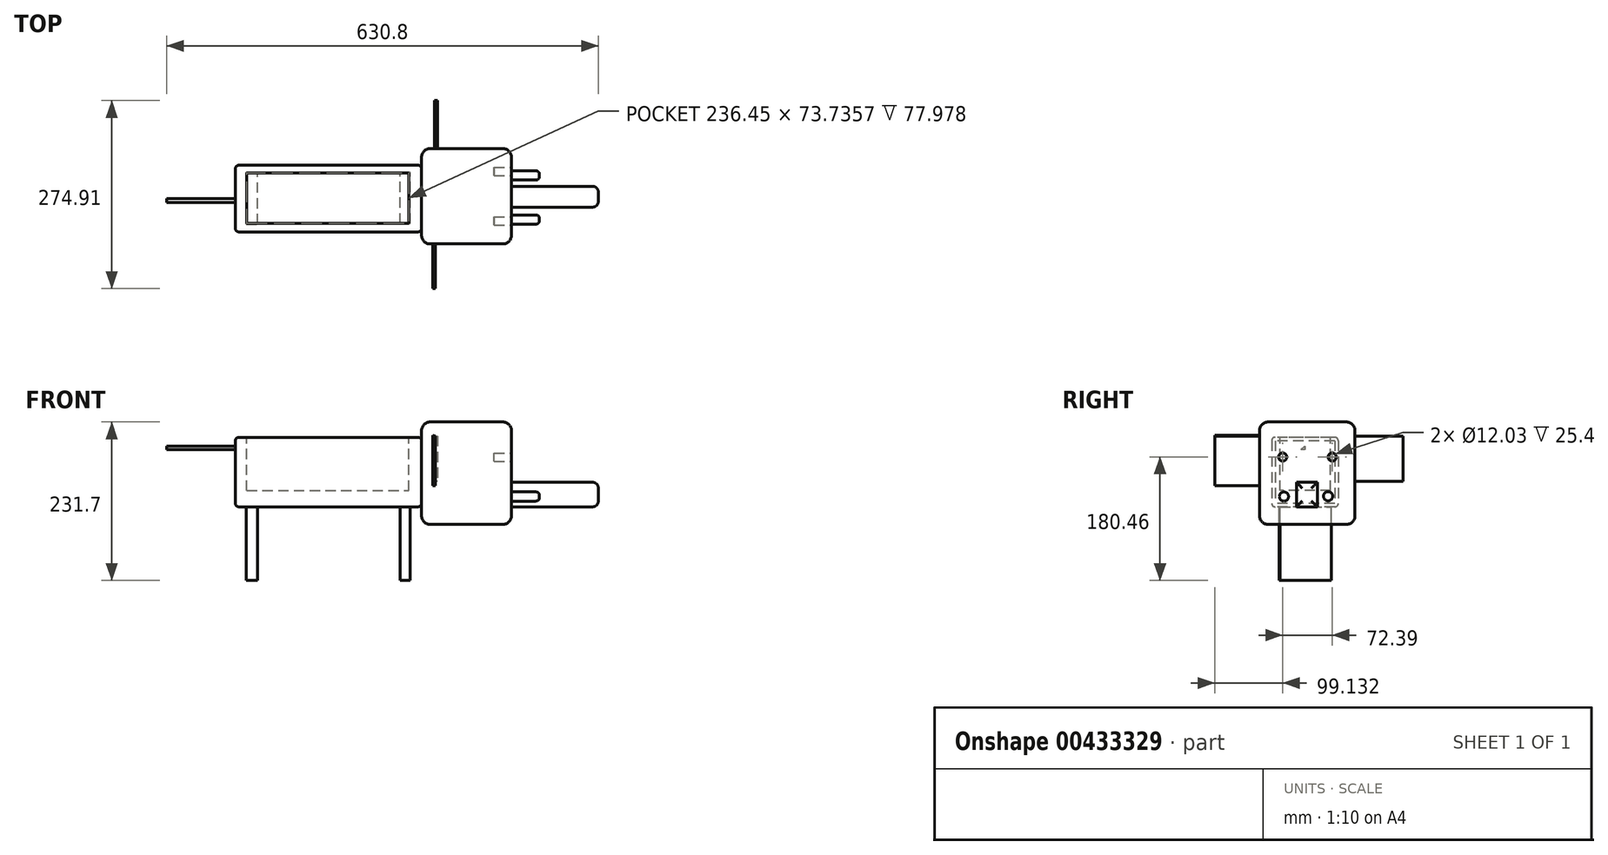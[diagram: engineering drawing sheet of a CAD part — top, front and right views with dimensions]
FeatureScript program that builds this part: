
annotation { "Feature Type Name" : "Feature", "Feature Type Description" : "" }
export const myFeature = defineFeature(function(context is Context, id is Id, definition is map)
    precondition{}
    {
        {
            var Q0;
            Q0=qCreatedBy(makeId("Top.planeOp"),FACE);
            var sketch = newSketch(context, id + "F0", { "sketchPlane" : qUnion([Q0])});
            skLineSegment(sketch, "E0.bottom", {"start": v(-125.37, 30.71) * mm, "end": v(146.52, 30.71) * mm});
            skLineSegment(sketch, "E0.top", {"start": v(-125.37, -66.73) * mm, "end": v(146.52, -66.73) * mm});
            skLineSegment(sketch, "E0.left", {"start": v(-125.37, 30.71) * mm, "end": v(-125.37, -66.73) * mm});
            skLineSegment(sketch, "E0.right", {"start": v(146.52, 30.71) * mm, "end": v(146.52, -66.73) * mm});
            skSolve(sketch);
        }
        {
            var Q0;
            Q0=makeQuery(id+"F0.imprint","IMPRINT",FACE,{"disambiguationData":[TD([[makeQuery(id+"F0.imprint","IMPRINT",EDGE,{"derivedFrom":sQuery(id+"F0.wireOp",EDGE,"E0.bottom")}),-1.0]])]});
            extrude(context, id + "F1", {"entities" : qUnion([Q0]), "depth" : 101.6 * mm});
        }
        {
            var Q0;
            Q0=makeQuery(id+"F1.opExtrude","CAP_FACE",FACE,{"disambiguationData":[OSD([sQuery(id+"F0.wireOp",EDGE,"E0.bottom"),sQuery(id+"F0.wireOp",EDGE,"E0.top"),sQuery(id+"F0.wireOp",EDGE,"E0.left"),sQuery(id+"F0.wireOp",EDGE,"E0.right")])],"isStart":false});
            var sketch = newSketch(context, id + "F2", { "sketchPlane" : qUnion([Q0])});
            skLineSegment(sketch, "E1.bottom", {"start": v(-108.8, 19.56) * mm, "end": v(127.65, 19.56) * mm});
            skLineSegment(sketch, "E1.top", {"start": v(-108.8, -54.18) * mm, "end": v(127.65, -54.18) * mm});
            skLineSegment(sketch, "E1.left", {"start": v(-108.8, 19.56) * mm, "end": v(-108.8, -54.18) * mm});
            skLineSegment(sketch, "E1.right", {"start": v(127.65, 19.56) * mm, "end": v(127.65, -54.18) * mm});
            skSolve(sketch);
        }
        {
            var Q0;
            Q0=makeQuery(id+"F1.opExtrude","SWEPT_FACE",FACE,{"disambiguationData":[OSD([sQuery(id+"F0.wireOp",EDGE,"E0.top")])]});
            var Q1;
            Q1=makeQuery(id+"F1.opExtrude","SWEPT_FACE",FACE,{"disambiguationData":[OSD([sQuery(id+"F0.wireOp",EDGE,"E0.right")])]});
            var Q2;
            Q2=makeQuery(id+"F1.opExtrude","SWEPT_FACE",FACE,{"disambiguationData":[OSD([sQuery(id+"F0.wireOp",EDGE,"E0.bottom")])]});
            var Q3;
            Q3=makeQuery(id+"F1.opExtrude","SWEPT_FACE",FACE,{"disambiguationData":[OSD([sQuery(id+"F0.wireOp",EDGE,"E0.left")])]});
            var Q4;
            Q4=makeQuery(id+"F95bG39HBBs5OQX_1.opShell","OFFSET_FACE",FACE,{"disambiguationData":[OSD([sQuery(id+"F0.wireOp",EDGE,"E0.top")])]});
            var Q5;
            Q5=makeQuery(id+"F95bG39HBBs5OQX_1.opShell","OFFSET_FACE",FACE,{"disambiguationData":[OSD([sQuery(id+"F0.wireOp",EDGE,"E0.left")])]});
            var Q6;
            Q6=makeQuery(id+"F95bG39HBBs5OQX_1.opShell","OFFSET_FACE",FACE,{"disambiguationData":[OSD([sQuery(id+"F0.wireOp",EDGE,"E0.bottom")])]});
            var Q7;
            Q7=makeQuery(id+"F95bG39HBBs5OQX_1.opShell","OFFSET_FACE",FACE,{"disambiguationData":[OSD([sQuery(id+"F0.wireOp",EDGE,"E0.bottom"),sQuery(id+"F0.wireOp",EDGE,"E0.top"),sQuery(id+"F0.wireOp",EDGE,"E0.left"),sQuery(id+"F0.wireOp",EDGE,"E0.right")])]});
            fillet(context, id + "F3", {"entities" : qUnion([Q0, Q1, Q2, Q3, Q4, Q5, Q6, Q7]), "radius" : 5.08 * mm, "tangentPropagation" : true, "allowEdgeOverflow" : false});
        }
        {
            var Q0;
            Q0=makeQuery(id+"F1.opExtrude","CAP_FACE",FACE,{"disambiguationData":[OSD([sQuery(id+"F0.wireOp",EDGE,"E0.bottom"),sQuery(id+"F0.wireOp",EDGE,"E0.top"),sQuery(id+"F0.wireOp",EDGE,"E0.left"),sQuery(id+"F0.wireOp",EDGE,"E0.right")])],"isStart":true});
            var sketch = newSketch(context, id + "F4", { "sketchPlane" : qUnion([Q0])});
            skLineSegment(sketch, "E2.bottom", {"start": v(-109.59, 55.4) * mm, "end": v(-92.98, 55.4) * mm});
            skLineSegment(sketch, "E2.top", {"start": v(-109.59, -20.61) * mm, "end": v(-92.98, -20.61) * mm});
            skLineSegment(sketch, "E2.left", {"start": v(-109.59, 55.4) * mm, "end": v(-109.59, -20.61) * mm});
            skLineSegment(sketch, "E2.right", {"start": v(-92.98, 55.4) * mm, "end": v(-92.98, -20.61) * mm});
            skSolve(sketch);
        }
        {
            var Q0;
            Q0 = qSketchRegion(id + "F4", true);
            extrude(context, id + "F5", {"entities" : qUnion([Q0]), "operationType" : NewBodyOperationType.ADD, "depth" : 107.7 * mm});
        }
        {
            var Q0;
            Q0=makeQuery(id+"F1.opExtrude","CAP_FACE",FACE,{"disambiguationData":[OSD([sQuery(id+"F0.wireOp",EDGE,"E0.bottom"),sQuery(id+"F0.wireOp",EDGE,"E0.top"),sQuery(id+"F0.wireOp",EDGE,"E0.left"),sQuery(id+"F0.wireOp",EDGE,"E0.right")])],"isStart":true});
            var sketch = newSketch(context, id + "F6", { "sketchPlane" : qUnion([Q0])});
            skLineSegment(sketch, "E3.bottom", {"start": v(115.1, 54.41) * mm, "end": v(130.15, 54.41) * mm});
            skLineSegment(sketch, "E3.top", {"start": v(115.1, -20.42) * mm, "end": v(130.15, -20.42) * mm});
            skLineSegment(sketch, "E3.left", {"start": v(115.1, 54.41) * mm, "end": v(115.1, -20.42) * mm});
            skLineSegment(sketch, "E3.right", {"start": v(130.15, 54.41) * mm, "end": v(130.15, -20.42) * mm});
            skSolve(sketch);
        }
        {
            var Q0;
            Q0 = qSketchRegion(id + "F6", true);
            extrude(context, id + "F7", {"entities" : qUnion([Q0]), "operationType" : NewBodyOperationType.ADD, "depth" : 107.7 * mm});
        }
        {
            var Q0;
            Q0 = qSketchRegion(id + "F2", true);
            extrude(context, id + "F8", {"entities" : qUnion([Q0]), "operationType" : NewBodyOperationType.REMOVE, "oppositeDirection" : true, "depth" : 77.98 * mm});
        }
        {
            var Q0;
            Q0=makeQuery(id+"F1.opExtrude","SWEPT_FACE",FACE,{"disambiguationData":[OSD([sQuery(id+"F0.wireOp",EDGE,"E0.right")])]});
            var sketch = newSketch(context, id + "F9", { "sketchPlane" : qUnion([Q0])});
            skLineSegment(sketch, "E4.bottom", {"start": v(-84.42, 124) * mm, "end": v(55.11, 124) * mm});
            skLineSegment(sketch, "E4.top", {"start": v(-84.42, -25.73) * mm, "end": v(55.11, -25.73) * mm});
            skLineSegment(sketch, "E4.left", {"start": v(-84.42, 124) * mm, "end": v(-84.42, -25.73) * mm});
            skLineSegment(sketch, "E4.right", {"start": v(55.11, 124) * mm, "end": v(55.11, -25.73) * mm});
            skSolve(sketch);
        }
        {
            var Q0;
            Q0 = qSketchRegion(id + "F9", true);
            extrude(context, id + "F10", {"entities" : qUnion([Q0]), "operationType" : NewBodyOperationType.ADD, "depth" : 131.32 * mm});
        }
        {
            var Q0;
            Q0=makeQuery(id+"F10.opExtrude","SWEPT_FACE",FACE,{"disambiguationData":[OSD([sQuery(id+"F9.wireOp",EDGE,"E4.bottom")])]});
            var Q1;
            Q1=makeQuery(id+"F10.opExtrude","SWEPT_FACE",FACE,{"disambiguationData":[OSD([sQuery(id+"F9.wireOp",EDGE,"E4.left")])]});
            var Q2;
            Q2=makeQuery(id+"F10.opExtrude","CAP_FACE",FACE,{"disambiguationData":[OSD([sQuery(id+"F9.wireOp",EDGE,"E4.bottom"),sQuery(id+"F9.wireOp",EDGE,"E4.top"),sQuery(id+"F9.wireOp",EDGE,"E4.left"),sQuery(id+"F9.wireOp",EDGE,"E4.right")])],"isStart":false});
            var Q3;
            Q3=makeQuery(id+"F10.opExtrude","SWEPT_FACE",FACE,{"disambiguationData":[OSD([sQuery(id+"F9.wireOp",EDGE,"E4.right")])]});
            var Q4;
            Q4=makeQuery(id+"F10.opExtrude","SWEPT_FACE",FACE,{"disambiguationData":[OSD([sQuery(id+"F9.wireOp",EDGE,"E4.top")])]});
            fillet(context, id + "F11", {"entities" : qUnion([Q0, Q1, Q2, Q3, Q4]), "radius" : 12.7 * mm, "tangentPropagation" : true, "allowEdgeOverflow" : false});
        }
        {
            var Q0;
            Q0=makeQuery(id+"F10.opExtrude","CAP_FACE",FACE,{"disambiguationData":[OSD([sQuery(id+"F9.wireOp",EDGE,"E4.bottom"),sQuery(id+"F9.wireOp",EDGE,"E4.top"),sQuery(id+"F9.wireOp",EDGE,"E4.left"),sQuery(id+"F9.wireOp",EDGE,"E4.right")])],"isStart":false});
            var sketch = newSketch(context, id + "F12", { "sketchPlane" : qUnion([Q0])});
            skLineSegment(sketch, "E5.bottom", {"start": v(-30.55, 35.93) * mm, "end": v(0, 35.93) * mm});
            skLineSegment(sketch, "E5.top", {"start": v(-30.55, 0) * mm, "end": v(0, 0) * mm});
            skLineSegment(sketch, "E5.left", {"start": v(-30.55, 35.93) * mm, "end": v(-30.55, 0) * mm});
            skLineSegment(sketch, "E5.right", {"start": v(0, 35.93) * mm, "end": v(0, 0) * mm});
            skSolve(sketch);
        }
        {
            var Q0;
            Q0 = qSketchRegion(id + "F12", true);
            extrude(context, id + "F13", {"entities" : qUnion([Q0]), "operationType" : NewBodyOperationType.ADD, "depth" : 127 * mm});
        }
        {
            var Q0;
            Q0=makeQuery(id+"F10.opExtrude","SWEPT_FACE",FACE,{"disambiguationData":[OSD([sQuery(id+"F9.wireOp",EDGE,"E4.left")])]});
            var sketch = newSketch(context, id + "F14", { "sketchPlane" : qUnion([Q0])});
            skLineSegment(sketch, "E6", {"start": v(163.04, 104.45) * mm, "end": v(163.04, 30.65) * mm});
            skLineSegment(sketch, "E7", {"start": v(163.04, 30.65) * mm, "end": v(166.6, 30.65) * mm});
            skLineSegment(sketch, "E8", {"start": v(166.6, 30.65) * mm, "end": v(166.6, 103.47) * mm});
            skLineSegment(sketch, "E9", {"start": v(166.6, 103.47) * mm, "end": v(163.04, 104.45) * mm});
            skSolve(sketch);
        }
        {
            var Q0;
            Q0=makeQuery(id+"F14.imprint","IMPRINT",FACE,{"disambiguationData":[TD([[makeQuery(id+"F14.imprint","IMPRINT",EDGE,{"derivedFrom":sQuery(id+"F14.wireOp",EDGE,"E6")}),1.0]])]});
            extrude(context, id + "F15", {"entities" : qUnion([Q0]), "operationType" : NewBodyOperationType.ADD, "depth" : 65.28 * mm});
        }
        {
            var Q0;
            Q0=makeQuery(id+"F10.opExtrude","SWEPT_FACE",FACE,{"disambiguationData":[OSD([sQuery(id+"F9.wireOp",EDGE,"E4.right")])]});
            var sketch = newSketch(context, id + "F16", { "sketchPlane" : qUnion([Q0])});
            skLineSegment(sketch, "E10", {"start": v(-165.3, 103.36) * mm, "end": v(-170, 103.36) * mm});
            skLineSegment(sketch, "E11", {"start": v(-170, 103.36) * mm, "end": v(-170, 36.95) * mm});
            skLineSegment(sketch, "E12", {"start": v(-170, 36.95) * mm, "end": v(-165.8, 36.95) * mm});
            skLineSegment(sketch, "E13", {"start": v(-165.8, 36.95) * mm, "end": v(-165.3, 103.36) * mm});
            skSolve(sketch);
        }
        {
            var Q0;
            Q0 = qSketchRegion(id + "F16", true);
            extrude(context, id + "F17", {"entities" : qUnion([Q0]), "operationType" : NewBodyOperationType.ADD, "depth" : 70.1 * mm});
        }
        {
            var Q0;
            Q0=makeQuery(id+"F10.opExtrude","CAP_FACE",FACE,{"disambiguationData":[OSD([sQuery(id+"F9.wireOp",EDGE,"E4.bottom"),sQuery(id+"F9.wireOp",EDGE,"E4.top"),sQuery(id+"F9.wireOp",EDGE,"E4.left"),sQuery(id+"F9.wireOp",EDGE,"E4.right")])],"isStart":false});
            var sketch = newSketch(context, id + "F18", { "sketchPlane" : qUnion([Q0])});
            skCircle(sketch, "E14", {"center": v(-48.64, 15.07) * mm, "radius": 6.72 * mm});
            skCircle(sketch, "E15.1.0.0", {"center": v(15.75, 15.5) * mm, "radius": 6.72 * mm});
            skLineSegment(sketch, "E15.direction1", {"start": v(-48.64, 15.07) * mm, "end": v(15.75, 15.5) * mm, "construction": true});
            skSolve(sketch);
        }
        {
            var Q0;
            Q0 = qSketchRegion(id + "F18", true);
            extrude(context, id + "F19", {"entities" : qUnion([Q0]), "operationType" : NewBodyOperationType.ADD, "depth" : 40.9 * mm});
        }
        {
            var Q0;
            Q0=makeQuery(id+"F1.opExtrude","SWEPT_FACE",FACE,{"disambiguationData":[OSD([sQuery(id+"F0.wireOp",EDGE,"E0.left")])]});
            var sketch = newSketch(context, id + "F20", { "sketchPlane" : qUnion([Q0])});
            skLineSegment(sketch, "E16", {"start": v(17.9, 88.55) * mm, "end": v(17.9, 83.87) * mm});
            skLineSegment(sketch, "E17", {"start": v(17.9, 83.87) * mm, "end": v(23.7, 83.87) * mm});
            skLineSegment(sketch, "E18", {"start": v(23.7, 83.87) * mm, "end": v(17.9, 88.55) * mm});
            skSolve(sketch);
        }
        {
            var Q0;
            Q0 = qSketchRegion(id + "F20", true);
            extrude(context, id + "F21", {"entities" : qUnion([Q0]), "operationType" : NewBodyOperationType.ADD, "depth" : 100.58 * mm});
        }
        {
            var Q0;
            Q0=makeQuery(id+"F10.opExtrude","CAP_FACE",FACE,{"disambiguationData":[OSD([sQuery(id+"F9.wireOp",EDGE,"E4.bottom"),sQuery(id+"F9.wireOp",EDGE,"E4.top"),sQuery(id+"F9.wireOp",EDGE,"E4.left"),sQuery(id+"F9.wireOp",EDGE,"E4.right")])],"isStart":false});
            var sketch = newSketch(context, id + "F22", { "sketchPlane" : qUnion([Q0])});
            skCircle(sketch, "E19", {"center": v(-50.56, 72.76) * mm, "radius": 6.01 * mm});
            skCircle(sketch, "E20.1.0.0", {"center": v(21.83, 72.76) * mm, "radius": 6.01 * mm});
            skLineSegment(sketch, "E20.direction1", {"start": v(-50.56, 72.76) * mm, "end": v(21.83, 72.76) * mm, "construction": true});
            skSolve(sketch);
        }
        {
            var Q0;
            Q0 = qSketchRegion(id + "F22", true);
            extrude(context, id + "F23", {"entities" : qUnion([Q0]), "operationType" : NewBodyOperationType.REMOVE, "oppositeDirection" : true, "depth" : 25.4 * mm});
        }
        {
            var Q0;
            Q0=makeQuery(id+"F19.opExtrude","CAP_FACE",FACE,{"disambiguationData":[OSD([sQuery(id+"F18.wireOp",EDGE,"E14")])],"isStart":false});
            var Q1;
            Q1=makeQuery(id+"F19.opExtrude","CAP_FACE",FACE,{"disambiguationData":[OSD([sQuery(id+"F18.wireOp",EDGE,"E15.1.0.0")])],"isStart":false});
            fillet(context, id + "F24", {"entities" : qUnion([Q0, Q1]), "radius" : 5.08 * mm, "tangentPropagation" : true, "allowEdgeOverflow" : false});
        }
        {
            var Q0;
            Q0=makeQuery(id+"F13.opExtrude","CAP_FACE",FACE,{"disambiguationData":[OSD([sQuery(id+"F12.wireOp",EDGE,"E5.bottom"),sQuery(id+"F12.wireOp",EDGE,"E5.top"),sQuery(id+"F12.wireOp",EDGE,"E5.left"),sQuery(id+"F12.wireOp",EDGE,"E5.right")])],"isStart":false});
            fillet(context, id + "F25", {"entities" : qUnion([Q0]), "radius" : 8.58 * mm, "tangentPropagation" : true, "allowEdgeOverflow" : false});
        }
    });
